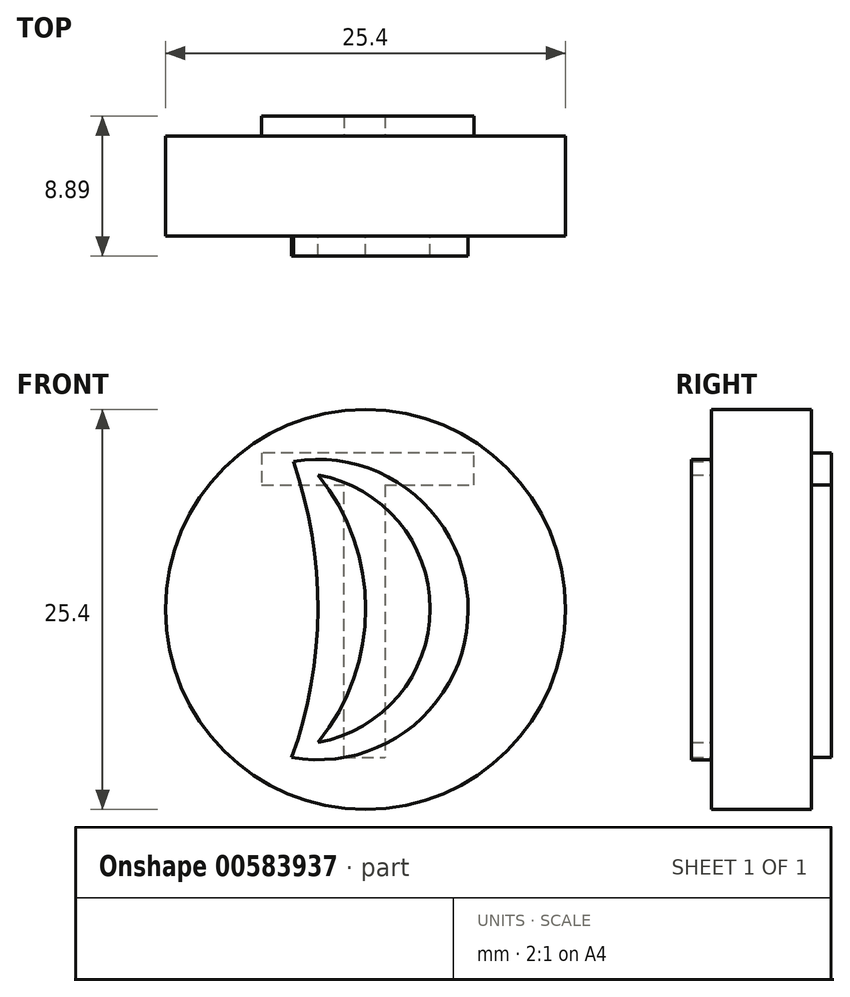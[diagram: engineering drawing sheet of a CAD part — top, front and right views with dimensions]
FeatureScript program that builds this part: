
annotation { "Feature Type Name" : "Feature", "Feature Type Description" : "" }
export const myFeature = defineFeature(function(context is Context, id is Id, definition is map)
    precondition{}
    {
        {
            var Q0;
            Q0=qCreatedBy(makeId("Front.planeOp"),FACE);
            var sketch = newSketch(context, id + "F0", { "sketchPlane" : qUnion([Q0])});
            skCircle(sketch, "E0", {"center": v(0, 0) * mm, "radius": 12.7 * mm});
            skSolve(sketch);
        }
        {
            var Q0;
            Q0=makeQuery(id+"F0.imprint","IMPRINT",FACE,{"disambiguationData":[TD([[makeQuery(id+"F0.imprint","IMPRINT",EDGE,{"derivedFrom":sQuery(id+"F0.wireOp",EDGE,"E0")}),1.0]])]});
            extrude(context, id + "F1", {"entities" : qUnion([Q0]), "depth" : 25.4 * mm, "offsetDistance" : 25.4 * mm});
        }
        {
            var Q0;
            Q0=makeQuery(id+"F1.opExtrude","CAP_FACE",FACE,{"disambiguationData":[OSD([sQuery(id+"F0.wireOp",EDGE,"E0")])],"isStart":false});
            extrude(context, id + "F2", {"entities" : qUnion([Q0]), "operationType" : NewBodyOperationType.REMOVE, "oppositeDirection" : true, "depth" : 19.05 * mm, "offsetDistance" : 25.4 * mm});
        }
        {
            var Q0;
            Q0=makeQuery(id+"F2.boolean.opBoolean","COPY",FACE,{"derivedFrom":makeQuery(id+"F2.opExtrude","CAP_FACE",FACE,{"disambiguationData":[OSD([sQuery(id+"F0.wireOp",EDGE,"E0")])],"isStart":false})});
            var sketch = newSketch(context, id + "F3", { "sketchPlane" : qUnion([Q0])});
            skArc(sketch, "E1", {"start": v(-4.69, -9.4) * mm, "mid": v(6.52, -0.06) * mm, "end": v(-4.59, 9.4) * mm});
            skArc(sketch, "E2", {"start": v(-4.69, -9.4) * mm, "mid": v(-3.02, 0) * mm, "end": v(-4.59, 9.4) * mm});
            skArc(sketch, "E3", {"start": v(-3.02, -8.45) * mm, "mid": v(0, 0.05) * mm, "end": v(-3.02, 8.55) * mm});
            skArc(sketch, "E4", {"start": v(-3.02, -8.45) * mm, "mid": v(4.1, 0.05) * mm, "end": v(-3.02, 8.55) * mm});
            skSolve(sketch);
        }
        {
            var Q0;
            Q0=makeQuery(id+"F3.imprint","IMPRINT",FACE,{"disambiguationData":[TD([[makeQuery(id+"F3.imprint","IMPRINT",EDGE,{"derivedFrom":sQuery(id+"F3.wireOp",EDGE,"E1")}),1.0]])]});
            extrude(context, id + "F4", {"entities" : qUnion([Q0]), "operationType" : NewBodyOperationType.ADD, "depth" : 1.27 * mm, "offsetDistance" : 25.4 * mm});
        }
        {
            var Q0;
            Q0=makeQuery(id+"F1.opExtrude","CAP_FACE",FACE,{"disambiguationData":[OSD([sQuery(id+"F0.wireOp",EDGE,"E0")])],"isStart":true});
            var sketch = newSketch(context, id + "F5", { "sketchPlane" : qUnion([Q0])});
            skLineSegment(sketch, "E5", {"start": v(-1.23, 0) * mm, "end": v(1.38, 0) * mm});
            skLineSegment(sketch, "E6", {"start": v(-1.23, 7.9) * mm, "end": v(-1.23, 0) * mm});
            skLineSegment(sketch, "E7", {"start": v(1.38, 0) * mm, "end": v(1.38, 7.9) * mm});
            skLineSegment(sketch, "E8", {"start": v(1.38, 7.9) * mm, "end": v(1.38, 0) * mm});
            skLineSegment(sketch, "E9", {"start": v(1.38, 0) * mm, "end": v(1.38, -9.4) * mm});
            skLineSegment(sketch, "E10", {"start": v(1.63, -9.4) * mm, "end": v(-1.23, -9.4) * mm});
            skLineSegment(sketch, "E11", {"start": v(-1.23, -9.4) * mm, "end": v(-1.23, 0) * mm});
            skLineSegment(sketch, "E12", {"start": v(-1.23, 7.9) * mm, "end": v(-6.9, 7.9) * mm});
            skLineSegment(sketch, "E13", {"start": v(-6.9, 7.6) * mm, "end": v(-6.9, 9.95) * mm});
            skLineSegment(sketch, "E14", {"start": v(-6.9, 9.95) * mm, "end": v(6.6, 9.95) * mm});
            skLineSegment(sketch, "E15", {"start": v(6.6, 9.95) * mm, "end": v(6.6, 7.9) * mm});
            skLineSegment(sketch, "E16", {"start": v(6.6, 7.9) * mm, "end": v(1.38, 7.9) * mm});
            skSolve(sketch);
        }
        {
            var Q0;
            Q0=makeQuery(id+"F5.imprint","IMPRINT",FACE,{"disambiguationData":[TD([[makeQuery(id+"F5.imprint","IMPRINT",EDGE,{"derivedFrom":sQuery(id+"F5.wireOp",EDGE,"E5")}),1.0]])]});
            var Q1;
            Q1=makeQuery(id+"F5.imprint","IMPRINT",FACE,{"disambiguationData":[TD([[makeQuery(id+"F5.imprint","IMPRINT",EDGE,{"derivedFrom":sQuery(id+"F5.wireOp",EDGE,"E5")}),-1.0]])]});
            extrude(context, id + "F6", {"entities" : qUnion([Q0, Q1]), "operationType" : NewBodyOperationType.ADD, "depth" : 1.27 * mm, "offsetDistance" : 25.4 * mm});
        }
    });
